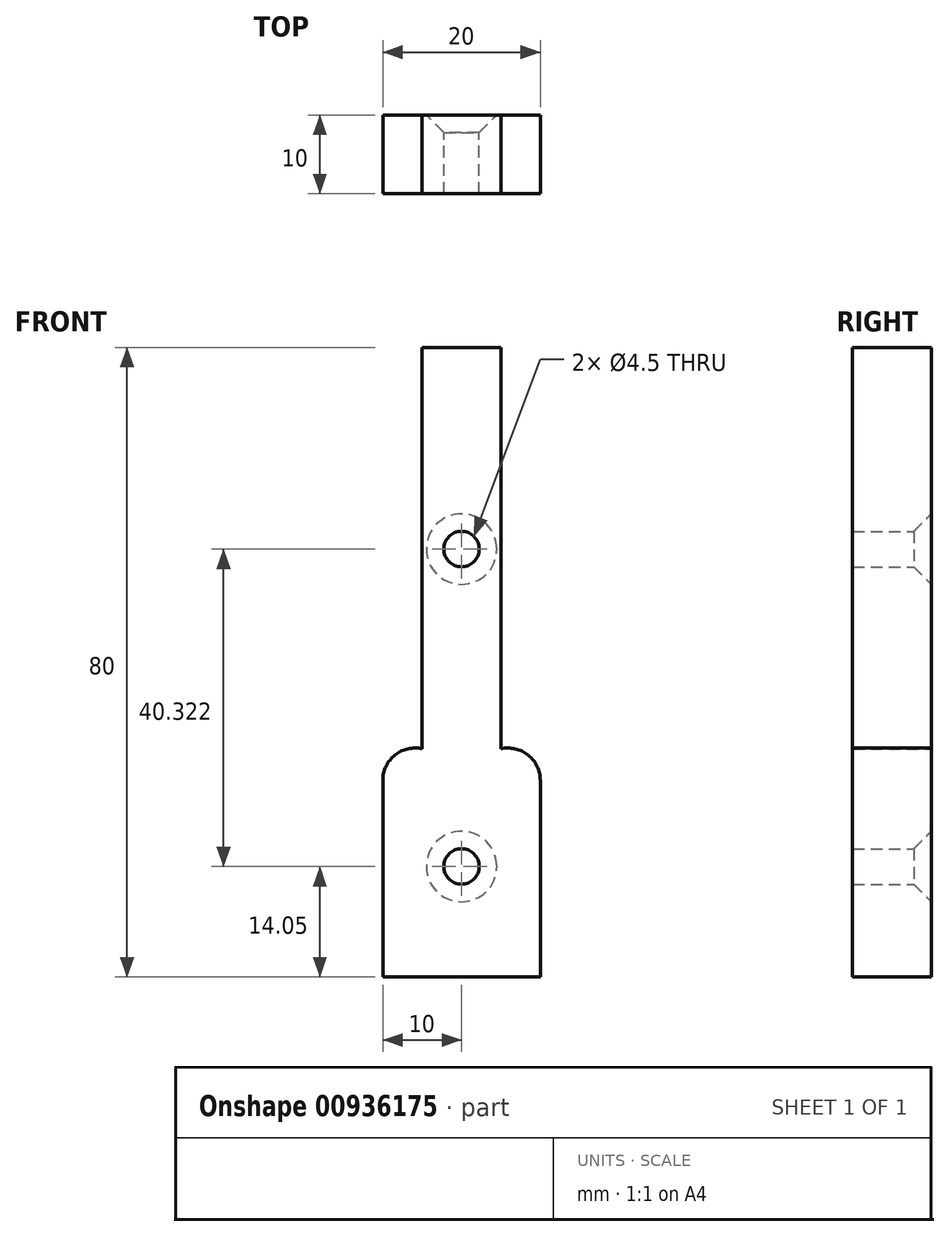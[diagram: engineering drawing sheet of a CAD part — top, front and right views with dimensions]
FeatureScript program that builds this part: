
annotation { "Feature Type Name" : "Feature", "Feature Type Description" : "" }
export const myFeature = defineFeature(function(context is Context, id is Id, definition is map)
    precondition{}
    {
        {
            var Q0;
            Q0=qCreatedBy(makeId("Front.planeOp"),FACE);
            var sketch = newSketch(context, id + "F0", { "sketchPlane" : qUnion([Q0])});
            skLineSegment(sketch, "E0.bottom", {"start": v(5, 40) * mm, "end": v(-5, 40) * mm});
            skLineSegment(sketch, "E0.top", {"start": v(5, -40) * mm, "end": v(-5, -40) * mm});
            skLineSegment(sketch, "E0.left", {"start": v(5, 40) * mm, "end": v(5, -40) * mm});
            skLineSegment(sketch, "E0.right", {"start": v(-5, 40) * mm, "end": v(-5, -40) * mm});
            skPoint(sketch, "E0.middle", {"position": v(0, 0) * mm});
            skLineSegment(sketch, "E1", {"start": v(-5, -40) * mm, "end": v(-10, -40) * mm});
            skLineSegment(sketch, "E2", {"start": v(-10, -40) * mm, "end": v(-10, -15) * mm});
            skPoint(sketch, "E3", {"position": v(-5, 40) * mm});
            skPoint(sketch, "E4", {"position": v(-5, -11) * mm});
            skArc(sketch, "E5", {"start": v(-10, -15) * mm, "mid": v(-8.46, -11.8) * mm, "end": v(-5, -11) * mm});
            skLineSegment(sketch, "E6", {"start": v(5, -40) * mm, "end": v(5, -15) * mm});
            skLineSegment(sketch, "E7.MirrorCS", {"start": v(10, -40) * mm, "end": v(10, -15) * mm});
            skArc(sketch, "E8.MirrorCS", {"start": v(10, -15) * mm, "mid": v(8.46, -11.8) * mm, "end": v(5, -11) * mm});
            skLineSegment(sketch, "E9.MirrorCS", {"start": v(5, -40) * mm, "end": v(10, -40) * mm});
            skPoint(sketch, "E10", {"position": v(0, 14.37) * mm});
            skPoint(sketch, "E11", {"position": v(0, -25.95) * mm});
            skPoint(sketch, "E11.positionSnap0", {"position": v(0, -40) * mm});
            skSolve(sketch);
        }
        {
            var Q0;
            Q0 = qSketchRegion(id + "F0", true);
            extrude(context, id + "F1", {"entities" : qUnion([Q0]), "depth" : 10 * mm, "offsetDistance" : 25 * mm});
        }
        {
            var Q0;
            Q0=sQuery(id+"F0.wireOp",VERTEX,"E10");
            var Q1;
            Q1=sQuery(id+"F0.wireOp",VERTEX,"E11");
            var Q2;
            Q2=makeQuery(id+"F1.opExtrude","SWEPT_BODY",BODY,{"disambiguationData":[OSD([sQuery(id+"F0.wireOp",EDGE,"E0.bottom"),sQuery(id+"F0.wireOp",EDGE,"E0.top"),sQuery(id+"F0.wireOp",EDGE,"E0.right"),sQuery(id+"F0.wireOp",EDGE,"E1"),sQuery(id+"F0.wireOp",EDGE,"E2"),sQuery(id+"F0.wireOp",EDGE,"E5"),sQuery(id+"F0.wireOp",EDGE,"E7.MirrorCS"),sQuery(id+"F0.wireOp",EDGE,"E8.MirrorCS"),sQuery(id+"F0.wireOp",EDGE,"E0.left"),sQuery(id+"F0.wireOp",EDGE,"E9.MirrorCS")])]});
            hole(context, id + "F2", {"style" : HoleStyle.C_SINK, "endStyle" : HoleEndStyle.THROUGH, "oppositeDirection" : true, "standardTappedOrClearance" : lookupTablePath({ "fit" : "Normal", "standard" : "ISO", "size" : "M4", "type" : "Clearance" }), "standardBlindInLast" : lookupTablePath({ "fit" : "Normal", "standard" : "ISO", "engagement" : "75%", "pitch" : "0.7 mm", "size" : "M4", "type" : "Clearance & tapped" }), "holeDiameter" : 4.5 * mm, "cSinkDiameter" : 8.96 * mm, "cSinkAngle" : 90 * degree, "majorDiameter" : 5 * mm, "isTappedThrough" : true, "tappedDepth" : 12 * mm, "tapClearance" : 3, "locations" : qUnion([Q0, Q1]), "scope" : qUnion([Q2])});
        }
    });
